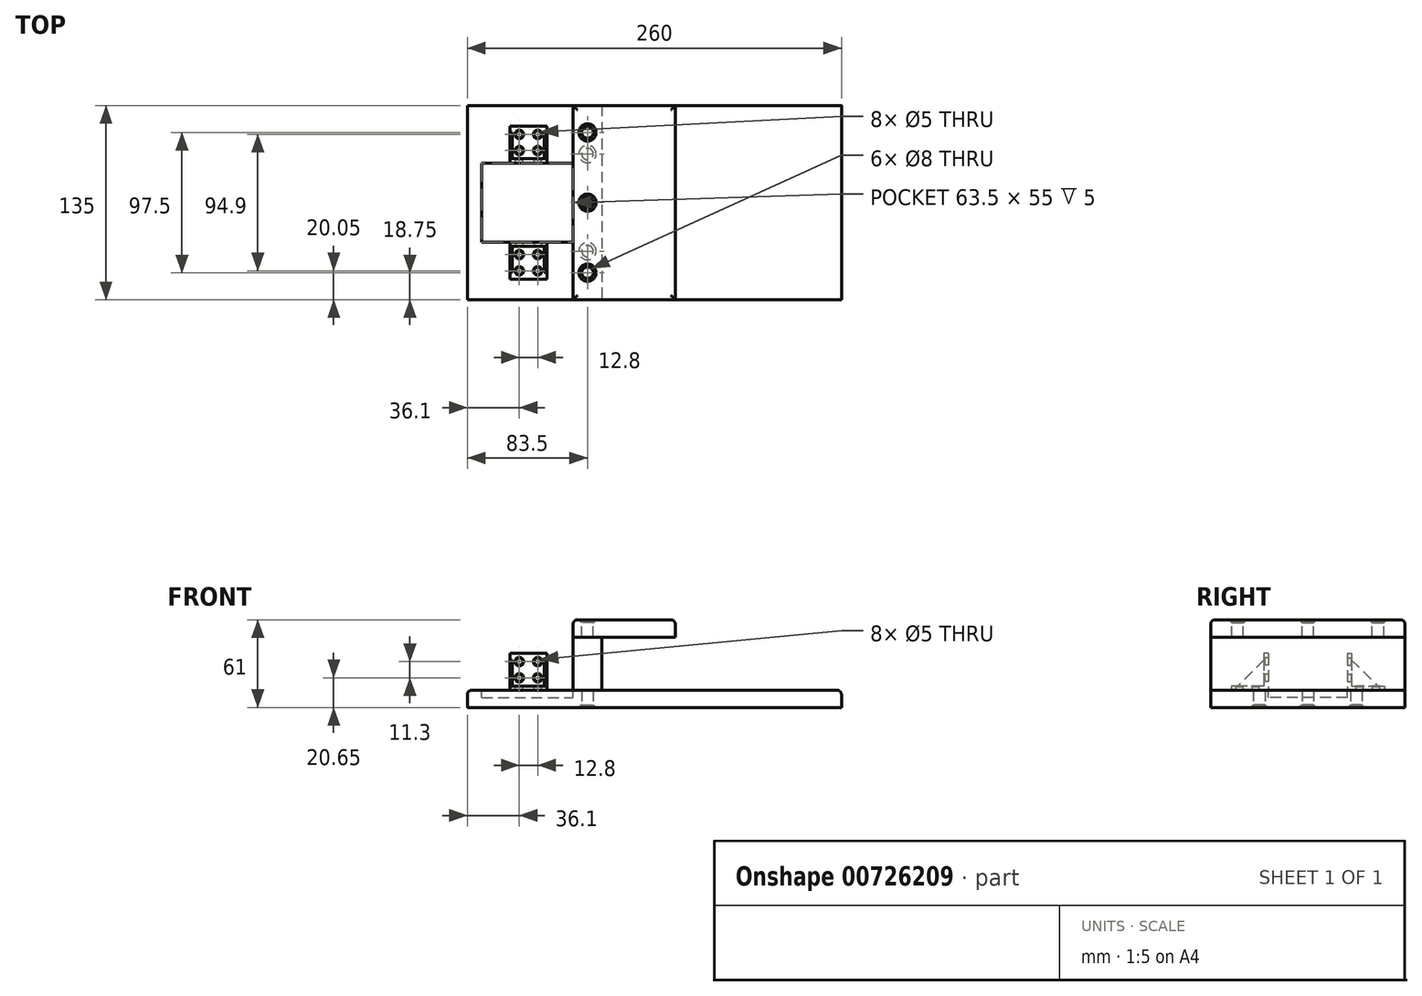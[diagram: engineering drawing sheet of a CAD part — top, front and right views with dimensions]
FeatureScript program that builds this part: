
annotation { "Feature Type Name" : "Feature", "Feature Type Description" : "" }
export const myFeature = defineFeature(function(context is Context, id is Id, definition is map)
    precondition{}
    {
        {
            var Q0;
            Q0=qCreatedBy(makeId("Top.planeOp"),FACE);
            var sketch = newSketch(context, id + "F0", { "sketchPlane" : qUnion([Q0])});
            skLineSegment(sketch, "E0.top", {"start": v(125, 67.5) * mm, "end": v(-125, 67.5) * mm});
            skLineSegment(sketch, "E0.left", {"start": v(125, -67.5) * mm, "end": v(125, 67.5) * mm});
            skPoint(sketch, "E0.middle", {"position": v(0, 0) * mm});
            skLineSegment(sketch, "E1.bottom", {"start": v(-125, 67.5) * mm, "end": v(-135, 67.5) * mm});
            skLineSegment(sketch, "E1.right", {"start": v(-135, 67.5) * mm, "end": v(-135, -67.5) * mm});
            skPoint(sketch, "E0.bottom.end.orphan", {"position": v(-125, -67.5) * mm});
            skLineSegment(sketch, "E2", {"start": v(125, -67.5) * mm, "end": v(-135, -67.5) * mm});
            skSolve(sketch);
        }
        {
            var Q0;
            Q0 = qSketchRegion(id + "F0", true);
            extrude(context, id + "F1", {"entities" : qUnion([Q0]), "endBound" : BoundingType.SYMMETRIC, "depth" : 12 * mm, "offsetDistance" : 25 * mm});
        }
        {
            var Q0;
            Q0=makeQuery(id+"F1.opExtrude","CAP_FACE",FACE,{"disambiguationData":[OSD([sQuery(id+"F0.wireOp",EDGE,"E0.bottom"),sQuery(id+"F0.wireOp",EDGE,"E0.top"),sQuery(id+"F0.wireOp",EDGE,"E0.left"),sQuery(id+"F0.wireOp",EDGE,"E0.right")])],"isStart":false});
            var sketch = newSketch(context, id + "F2", { "sketchPlane" : qUnion([Q0])});
            skLineSegment(sketch, "E3.bottom", {"start": v(-125, 27.5) * mm, "end": v(-61.5, 27.5) * mm});
            skLineSegment(sketch, "E3.top", {"start": v(-125, -27.5) * mm, "end": v(-61.5, -27.5) * mm});
            skLineSegment(sketch, "E3.left", {"start": v(-125, 27.5) * mm, "end": v(-125, -27.5) * mm});
            skLineSegment(sketch, "E3.right", {"start": v(-61.5, 27.5) * mm, "end": v(-61.5, -27.5) * mm});
            skSolve(sketch);
        }
        {
            var Q0;
            Q0 = qSketchRegion(id + "F2", true);
            extrude(context, id + "F3", {"entities" : qUnion([Q0]), "operationType" : NewBodyOperationType.REMOVE, "oppositeDirection" : true, "depth" : 5 * mm, "offsetDistance" : 25 * mm});
        }
        {
            var Q0;
            Q0=makeQuery(id+"F1.opExtrude","CAP_FACE",FACE,{"disambiguationData":[OSD([sQuery(id+"F0.wireOp",EDGE,"E0.bottom"),sQuery(id+"F0.wireOp",EDGE,"E0.top"),sQuery(id+"F0.wireOp",EDGE,"E0.left"),sQuery(id+"F0.wireOp",EDGE,"E0.right")])],"isStart":false});
            var sketch = newSketch(context, id + "F4", { "sketchPlane" : qUnion([Q0])});
            skLineSegment(sketch, "E4.bottom", {"start": v(-61.5, 67.5) * mm, "end": v(-41.5, 67.5) * mm});
            skLineSegment(sketch, "E4.top", {"start": v(-61.5, -67.5) * mm, "end": v(-41.5, -67.5) * mm});
            skLineSegment(sketch, "E4.left", {"start": v(-61.5, 67.5) * mm, "end": v(-61.5, -67.5) * mm});
            skLineSegment(sketch, "E4.right", {"start": v(-41.5, 67.5) * mm, "end": v(-41.5, -67.5) * mm});
            skSolve(sketch);
        }
        {
            var Q0;
            Q0 = qSketchRegion(id + "F4", true);
            extrude(context, id + "F5", {"entities" : qUnion([Q0]), "depth" : 37 * mm, "offsetDistance" : 25 * mm});
        }
        {
            var Q0;
            Q0=makeQuery(id+"F1.opExtrude","CAP_FACE",FACE,{"disambiguationData":[OSD([sQuery(id+"F0.wireOp",EDGE,"E0.bottom"),sQuery(id+"F0.wireOp",EDGE,"E0.top"),sQuery(id+"F0.wireOp",EDGE,"E0.left"),sQuery(id+"F0.wireOp",EDGE,"E0.right")])],"isStart":true});
            var sketch = newSketch(context, id + "F6", { "sketchPlane" : qUnion([Q0])});
            skLineSegment(sketch, "E5", {"start": v(-51.5, 67.5) * mm, "end": v(-51.5, -67.5) * mm});
            skCircle(sketch, "E6", {"center": v(-51.5, -33.75) * mm, "radius": 4 * mm});
            skCircle(sketch, "E7", {"center": v(-51.5, 33.75) * mm, "radius": 4 * mm});
            skCircle(sketch, "E8", {"center": v(-51.5, 0) * mm, "radius": 4 * mm});
            skSolve(sketch);
        }
        {
            var Q0;
            Q0=sQuery(id+"F6.wireOp",VERTEX,"E7.center");
            var Q1;
            Q1=sQuery(id+"F6.wireOp",VERTEX,"E8.center");
            var Q2;
            Q2=sQuery(id+"F6.wireOp",VERTEX,"E6.center");
            var Q3;
            Q3=makeQuery(id+"F1.opExtrude","SWEPT_BODY",BODY,{"disambiguationData":[OSD([sQuery(id+"F0.wireOp",EDGE,"E0.bottom"),sQuery(id+"F0.wireOp",EDGE,"E0.top"),sQuery(id+"F0.wireOp",EDGE,"E0.left"),sQuery(id+"F0.wireOp",EDGE,"E0.right")])]});
            hole(context, id + "F7", {"style" : HoleStyle.C_SINK, "endStyle" : HoleEndStyle.BLIND, "holeDiameter" : 8 * mm, "cSinkDiameter" : 12 * mm, "cSinkAngle" : 90 * degree, "majorDiameter" : 5 * mm, "holeDepth" : 12 * mm, "isTappedThrough" : true, "tappedDepth" : 12 * mm, "tapClearance" : 3, "locations" : qUnion([Q0, Q1, Q2]), "scope" : qUnion([Q3])});
        }
        {
            var Q0;
            Q0=makeQuery(id+"F5.opExtrude","CAP_FACE",FACE,{"disambiguationData":[OSD([sQuery(id+"F4.wireOp",EDGE,"E4.bottom"),sQuery(id+"F4.wireOp",EDGE,"E4.top"),sQuery(id+"F4.wireOp",EDGE,"E4.left"),sQuery(id+"F4.wireOp",EDGE,"E4.right")])],"isStart":false});
            var sketch = newSketch(context, id + "F8", { "sketchPlane" : qUnion([Q0])});
            skLineSegment(sketch, "E9.bottom", {"start": v(-61.5, 67.5) * mm, "end": v(9.5, 67.5) * mm});
            skLineSegment(sketch, "E9.top", {"start": v(-61.5, -67.5) * mm, "end": v(9.5, -67.5) * mm});
            skLineSegment(sketch, "E9.left", {"start": v(-61.5, 67.5) * mm, "end": v(-61.5, -67.5) * mm});
            skLineSegment(sketch, "E9.right", {"start": v(9.5, 67.5) * mm, "end": v(9.5, -67.5) * mm});
            skSolve(sketch);
        }
        {
            var Q0;
            Q0 = qSketchRegion(id + "F8", true);
            extrude(context, id + "F9", {"entities" : qUnion([Q0]), "depth" : 12 * mm, "offsetDistance" : 25 * mm});
        }
        {
            var Q0;
            Q0=makeQuery(id+"F9.opExtrude","CAP_FACE",FACE,{"disambiguationData":[OSD([sQuery(id+"F8.wireOp",EDGE,"E9.bottom"),sQuery(id+"F8.wireOp",EDGE,"E9.top"),sQuery(id+"F8.wireOp",EDGE,"E9.left"),sQuery(id+"F8.wireOp",EDGE,"E9.right")])],"isStart":false});
            var sketch = newSketch(context, id + "F10", { "sketchPlane" : qUnion([Q0])});
            skLineSegment(sketch, "E10", {"start": v(-51.5, 67.5) * mm, "end": v(-51.5, -67.5) * mm});
            skCircle(sketch, "E11", {"center": v(-51.5, 0) * mm, "radius": 5.3 * mm});
            skCircle(sketch, "E12", {"center": v(-51.5, 48.75) * mm, "radius": 5.83 * mm});
            skCircle(sketch, "E13.MirrorC", {"center": v(-51.5, -48.75) * mm, "radius": 5.83 * mm});
            skSolve(sketch);
        }
        {
            var Q0;
            Q0=sQuery(id+"F10.wireOp",VERTEX,"E12.center");
            var Q1;
            Q1=sQuery(id+"F10.wireOp",VERTEX,"E11.center");
            var Q2;
            Q2=sQuery(id+"F10.wireOp",VERTEX,"E13.MirrorC.center");
            var Q3;
            Q3=makeQuery(id+"F9.opExtrude","SWEPT_BODY",BODY,{"disambiguationData":[OSD([sQuery(id+"F8.wireOp",EDGE,"E9.bottom"),sQuery(id+"F8.wireOp",EDGE,"E9.top"),sQuery(id+"F8.wireOp",EDGE,"E9.left"),sQuery(id+"F8.wireOp",EDGE,"E9.right")])]});
            hole(context, id + "F11", {"style" : HoleStyle.C_SINK, "endStyle" : HoleEndStyle.BLIND, "holeDiameter" : 8 * mm, "cSinkDiameter" : 12 * mm, "cSinkAngle" : 90 * degree, "majorDiameter" : 5 * mm, "holeDepth" : 12 * mm, "isTappedThrough" : true, "tappedDepth" : 12 * mm, "tapClearance" : 3, "locations" : qUnion([Q0, Q1, Q2]), "scope" : qUnion([Q3])});
        }
        {
            var Q0;
            Q0=makeQuery(id+"F1.opExtrude","CAP_EDGE",EDGE,{"disambiguationData":[OSD([sQuery(id+"F0.wireOp",EDGE,"E0.right")])],"isStart":false});
            var Q1;
            Q1=makeQuery(id+"F1.opExtrude","CAP_EDGE",EDGE,{"disambiguationData":[OSD([sQuery(id+"F0.wireOp",EDGE,"E0.left")])],"isStart":false});
            var Q2;
            Q2=makeQuery(id+"F9.opExtrude","CAP_EDGE",EDGE,{"disambiguationData":[OSD([sQuery(id+"F8.wireOp",EDGE,"E9.right")])],"isStart":false});
            var Q3;
            Q3=makeQuery(id+"F9.opExtrude","CAP_EDGE",EDGE,{"disambiguationData":[OSD([sQuery(id+"F8.wireOp",EDGE,"E9.top")])],"isStart":false});
            var Q4;
            Q4=makeQuery(id+"F9.opExtrude","CAP_EDGE",EDGE,{"disambiguationData":[OSD([sQuery(id+"F8.wireOp",EDGE,"E9.bottom")])],"isStart":false});
            var Q5;
            Q5=makeQuery(id+"F9.opExtrude","CAP_EDGE",EDGE,{"disambiguationData":[OSD([sQuery(id+"F8.wireOp",EDGE,"E9.left")])],"isStart":false});
            var Q6;
            Q6=makeQuery(id+"F1.opExtrude","CAP_EDGE",EDGE,{"disambiguationData":[OSD([sQuery(id+"F0.wireOp",EDGE,"E1.right")])],"isStart":false});
            fillet(context, id + "F12", {"entities" : qUnion([Q0, Q1, Q2, Q3, Q4, Q5, Q6]), "radius" : 3 * mm, "tangentPropagation" : true, "allowEdgeOverflow" : false});
        }
        {
            var Q0;
            Q0=makeQuery(id+"F1.opExtrude","CAP_FACE",FACE,{"disambiguationData":[OSD([sQuery(id+"F0.wireOp",EDGE,"E0.top"),sQuery(id+"F0.wireOp",EDGE,"E0.left"),sQuery(id+"F0.wireOp",EDGE,"E1.bottom"),sQuery(id+"F0.wireOp",EDGE,"E1.right"),sQuery(id+"F0.wireOp",EDGE,"E2")])],"isStart":false});
            var sketch = newSketch(context, id + "F13", { "sketchPlane" : qUnion([Q0])});
            skLineSegment(sketch, "E14.bottom", {"start": v(-105.3, 27.5) * mm, "end": v(-79.7, 27.5) * mm});
            skLineSegment(sketch, "E14.top", {"start": v(-105.3, 53.1) * mm, "end": v(-79.7, 53.1) * mm});
            skLineSegment(sketch, "E14.left", {"start": v(-105.3, 27.5) * mm, "end": v(-105.3, 53.1) * mm});
            skLineSegment(sketch, "E14.right", {"start": v(-79.7, 27.5) * mm, "end": v(-79.7, 53.1) * mm});
            skSolve(sketch);
        }
        {
            var Q0;
            Q0 = qSketchRegion(id + "F13", true);
            extrude(context, id + "F14", {"entities" : qUnion([Q0]), "depth" : 3 * mm, "offsetDistance" : 25 * mm});
        }
        {
            var Q0;
            Q0=makeQuery(id+"F14.opExtrude","CAP_FACE",FACE,{"disambiguationData":[OSD([sQuery(id+"F13.wireOp",EDGE,"E14.bottom"),sQuery(id+"F13.wireOp",EDGE,"E14.top"),sQuery(id+"F13.wireOp",EDGE,"E14.left"),sQuery(id+"F13.wireOp",EDGE,"E14.right")])],"isStart":false});
            var sketch = newSketch(context, id + "F15", { "sketchPlane" : qUnion([Q0])});
            skLineSegment(sketch, "E15.bottom", {"start": v(-79.7, 27.5) * mm, "end": v(-105.3, 27.5) * mm});
            skLineSegment(sketch, "E15.top", {"start": v(-79.7, 30.5) * mm, "end": v(-105.3, 30.5) * mm});
            skLineSegment(sketch, "E15.left", {"start": v(-79.7, 27.5) * mm, "end": v(-79.7, 30.5) * mm});
            skLineSegment(sketch, "E15.right", {"start": v(-105.3, 27.5) * mm, "end": v(-105.3, 30.5) * mm});
            skSolve(sketch);
        }
        {
            var Q0;
            Q0 = qSketchRegion(id + "F15", true);
            extrude(context, id + "F16", {"entities" : qUnion([Q0]), "operationType" : NewBodyOperationType.ADD, "depth" : 22.6 * mm, "offsetDistance" : 25 * mm});
        }
        {
            var Q0;
            Q0=makeQuery(id+"F16.opExtrude","SWEPT_FACE",FACE,{"disambiguationData":[OSD([sQuery(id+"F15.wireOp",EDGE,"E15.top")])]});
            var sketch = newSketch(context, id + "F17", { "sketchPlane" : qUnion([Q0])});
            skLineSegment(sketch, "E16", {"start": v(92.5, 31.6) * mm, "end": v(92.5, 9) * mm});
            skLineSegment(sketch, "E17", {"start": v(92.5, 9) * mm, "end": v(105.3, 20.3) * mm});
            skLineSegment(sketch, "E18", {"start": v(105.3, 20.3) * mm, "end": v(92.5, 31.6) * mm});
            skPoint(sketch, "E19", {"position": v(98.9, 25.95) * mm});
            skPoint(sketch, "E20", {"position": v(98.9, 14.65) * mm});
            skPoint(sketch, "E21", {"position": v(92.5, 20.3) * mm});
            skPoint(sketch, "E22.MirrorP", {"position": v(86.1, 25.95) * mm});
            skPoint(sketch, "E23.MirrorP", {"position": v(86.1, 14.65) * mm});
            skSolve(sketch);
        }
        {
            var Q0;
            Q0=sQuery(id+"F17.wireOp",VERTEX,"E22.MirrorP");
            var Q1;
            Q1=sQuery(id+"F17.wireOp",VERTEX,"E19");
            var Q2;
            Q2=sQuery(id+"F17.wireOp",VERTEX,"E23.MirrorP");
            var Q3;
            Q3=sQuery(id+"F17.wireOp",VERTEX,"E20");
            var Q4;
            Q4=makeQuery(id+"F14.opExtrude","SWEPT_BODY",BODY,{"disambiguationData":[OSD([sQuery(id+"F13.wireOp",EDGE,"E14.bottom"),sQuery(id+"F13.wireOp",EDGE,"E14.top"),sQuery(id+"F13.wireOp",EDGE,"E14.left"),sQuery(id+"F13.wireOp",EDGE,"E14.right")])]});
            hole(context, id + "F18", {"style" : HoleStyle.C_SINK, "endStyle" : HoleEndStyle.BLIND, "holeDiameter" : 5 * mm, "cSinkDiameter" : 6 * mm, "cSinkAngle" : 90 * degree, "majorDiameter" : 5 * mm, "holeDepth" : 3 * mm, "isTappedThrough" : true, "tappedDepth" : 12 * mm, "tapClearance" : 3, "locations" : qUnion([Q0, Q1, Q2, Q3]), "scope" : qUnion([Q4])});
        }
        {
            var Q0;
            Q0=makeQuery(id+"F14.opExtrude","CAP_FACE",FACE,{"disambiguationData":[OSD([sQuery(id+"F13.wireOp",EDGE,"E14.bottom"),sQuery(id+"F13.wireOp",EDGE,"E14.top"),sQuery(id+"F13.wireOp",EDGE,"E14.left"),sQuery(id+"F13.wireOp",EDGE,"E14.right")])],"isStart":false});
            var sketch = newSketch(context, id + "F19", { "sketchPlane" : qUnion([Q0])});
            skLineSegment(sketch, "E24", {"start": v(-92.5, 30.5) * mm, "end": v(-92.5, 53.1) * mm});
            skLineSegment(sketch, "E25", {"start": v(-92.5, 53.1) * mm, "end": v(-105.3, 41.8) * mm});
            skLineSegment(sketch, "E26", {"start": v(-105.3, 41.8) * mm, "end": v(-92.5, 30.5) * mm});
            skPoint(sketch, "E27", {"position": v(-92.5, 41.8) * mm});
            skPoint(sketch, "E28", {"position": v(-98.9, 36.15) * mm});
            skPoint(sketch, "E29", {"position": v(-98.9, 47.45) * mm});
            skPoint(sketch, "E30.MirrorP", {"position": v(-86.1, 36.15) * mm});
            skPoint(sketch, "E31.MirrorP", {"position": v(-86.1, 47.45) * mm});
            skSolve(sketch);
        }
        {
            var Q0;
            Q0=sQuery(id+"F19.wireOp",VERTEX,"E30.MirrorP");
            var Q1;
            Q1=sQuery(id+"F19.wireOp",VERTEX,"E28");
            var Q2;
            Q2=sQuery(id+"F19.wireOp",VERTEX,"E29");
            var Q3;
            Q3=sQuery(id+"F19.wireOp",VERTEX,"E31.MirrorP");
            var Q4;
            Q4=makeQuery(id+"F14.opExtrude","SWEPT_BODY",BODY,{"disambiguationData":[OSD([sQuery(id+"F13.wireOp",EDGE,"E14.bottom"),sQuery(id+"F13.wireOp",EDGE,"E14.top"),sQuery(id+"F13.wireOp",EDGE,"E14.left"),sQuery(id+"F13.wireOp",EDGE,"E14.right")])]});
            hole(context, id + "F20", {"style" : HoleStyle.C_SINK, "endStyle" : HoleEndStyle.BLIND, "holeDiameter" : 5 * mm, "cSinkDiameter" : 6 * mm, "cSinkAngle" : 90 * degree, "majorDiameter" : 5 * mm, "holeDepth" : 3 * mm, "isTappedThrough" : true, "tappedDepth" : 12 * mm, "tapClearance" : 3, "locations" : qUnion([Q0, Q1, Q2, Q3]), "scope" : qUnion([Q4])});
        }
        {
            var Q0;
            Q0=makeQuery(id+"F16.boolean.opBoolean","MERGE",FACE,{"derivedFrom":[makeQuery(id+"F14.opExtrude","SWEPT_FACE",FACE,{"disambiguationData":[OSD([sQuery(id+"F13.wireOp",EDGE,"E14.left")])]}),makeQuery(id+"F16.opExtrude","SWEPT_FACE",FACE,{"disambiguationData":[OSD([sQuery(id+"F15.wireOp",EDGE,"E15.right")])]})]});
            var sketch = newSketch(context, id + "F21", { "sketchPlane" : qUnion([Q0])});
            skLineSegment(sketch, "E32", {"start": v(-30.5, 27.1) * mm, "end": v(-48.6, 9) * mm});
            skLineSegment(sketch, "E33", {"start": v(-48.6, 9) * mm, "end": v(-30.5, 9) * mm});
            skLineSegment(sketch, "E34", {"start": v(-30.5, 9) * mm, "end": v(-30.5, 27.1) * mm});
            skSolve(sketch);
        }
        {
            var Q0;
            Q0 = qSketchRegion(id + "F21", true);
            extrude(context, id + "F22", {"entities" : qUnion([Q0]), "operationType" : NewBodyOperationType.ADD, "oppositeDirection" : true, "depth" : 1.5 * mm, "offsetDistance" : 25 * mm});
        }
        {
            var Q0;
            Q0=makeQuery(id+"F16.boolean.opBoolean","MERGE",FACE,{"derivedFrom":[makeQuery(id+"F14.opExtrude","SWEPT_FACE",FACE,{"disambiguationData":[OSD([sQuery(id+"F13.wireOp",EDGE,"E14.right")])]}),makeQuery(id+"F16.opExtrude","SWEPT_FACE",FACE,{"disambiguationData":[OSD([sQuery(id+"F15.wireOp",EDGE,"E15.left")])]})]});
            var sketch = newSketch(context, id + "F23", { "sketchPlane" : qUnion([Q0])});
            skLineSegment(sketch, "E35", {"start": v(30.5, 9) * mm, "end": v(48.6, 9) * mm});
            skLineSegment(sketch, "E36", {"start": v(48.6, 9) * mm, "end": v(30.5, 27.1) * mm});
            skLineSegment(sketch, "E37", {"start": v(30.5, 27.1) * mm, "end": v(30.5, 9) * mm});
            skSolve(sketch);
        }
        {
            var Q0;
            Q0 = qSketchRegion(id + "F23", true);
            extrude(context, id + "F24", {"entities" : qUnion([Q0]), "operationType" : NewBodyOperationType.ADD, "oppositeDirection" : true, "depth" : 2 * mm, "offsetDistance" : 25 * mm});
        }
        {
            var Q0;
            Q0=makeQuery(id+"F14.opExtrude","SWEPT_BODY",BODY,{"disambiguationData":[OSD([sQuery(id+"F13.wireOp",EDGE,"E14.bottom"),sQuery(id+"F13.wireOp",EDGE,"E14.top"),sQuery(id+"F13.wireOp",EDGE,"E14.left"),sQuery(id+"F13.wireOp",EDGE,"E14.right")])]});
            var Q1;
            Q1=qCreatedBy(makeId("Front.planeOp"),FACE);
            mirror(context, id + "F25", {"entities" : qUnion([Q0]), "mirrorPlane" : qUnion([Q1])});
        }
    });
